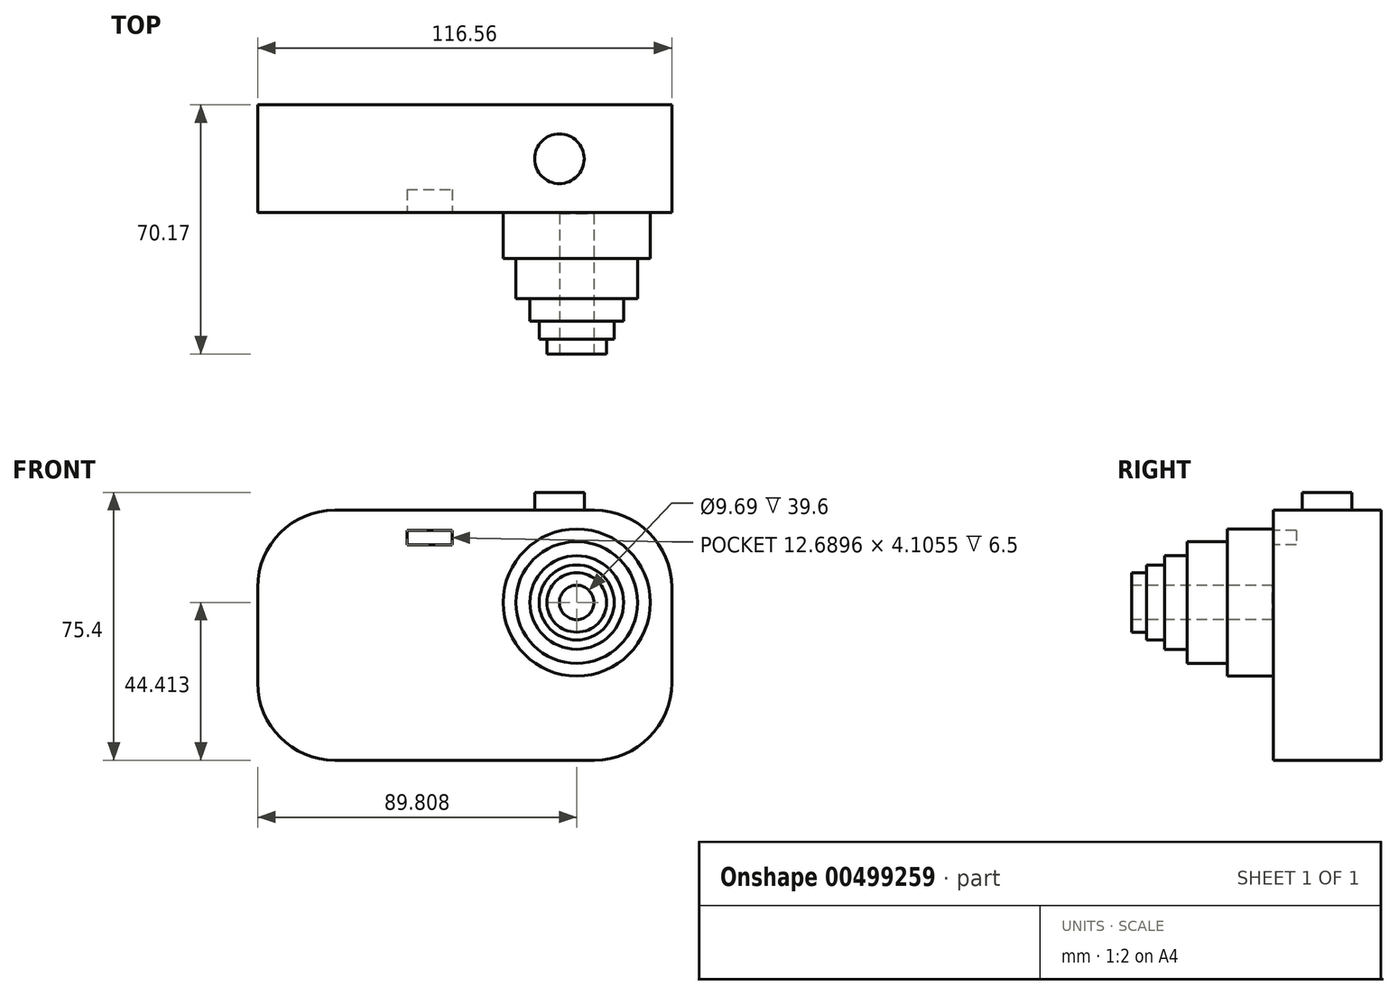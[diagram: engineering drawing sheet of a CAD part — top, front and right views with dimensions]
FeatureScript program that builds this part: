
annotation { "Feature Type Name" : "Feature", "Feature Type Description" : "" }
export const myFeature = defineFeature(function(context is Context, id is Id, definition is map)
    precondition{}
    {
        {
            var Q0;
            Q0=qCreatedBy(makeId("Top.planeOp"),FACE);
            var sketch = newSketch(context, id + "F0", { "sketchPlane" : qUnion([Q0])});
            skLineSegment(sketch, "E0.bottom", {"start": v(0, 0) * mm, "end": v(-116.56, 0) * mm});
            skLineSegment(sketch, "E0.top", {"start": v(0, 30.37) * mm, "end": v(-116.56, 30.37) * mm});
            skLineSegment(sketch, "E0.left", {"start": v(0, 0) * mm, "end": v(0, 30.37) * mm});
            skLineSegment(sketch, "E0.right", {"start": v(-116.56, 0) * mm, "end": v(-116.56, 30.37) * mm});
            skSolve(sketch);
        }
        {
            var Q0;
            Q0=makeQuery(id+"F0.imprint","IMPRINT",FACE,{"disambiguationData":[TD([[makeQuery(id+"F0.imprint","IMPRINT",EDGE,{"derivedFrom":sQuery(id+"F0.wireOp",EDGE,"E0.bottom")}),-1.0]])]});
            extrude(context, id + "F1", {"entities" : qUnion([Q0]), "depth" : 70.4 * mm});
        }
        {
            var Q0;
            Q0=makeQuery(id+"F1.opExtrude","CAP_EDGE",EDGE,{"disambiguationData":[OSD([sQuery(id+"F0.wireOp",EDGE,"E0.right")])],"isStart":false});
            var Q1;
            Q1=makeQuery(id+"F1.opExtrude","CAP_EDGE",EDGE,{"disambiguationData":[OSD([sQuery(id+"F0.wireOp",EDGE,"E0.left")])],"isStart":false});
            var Q2;
            Q2=makeQuery(id+"F1.opExtrude","CAP_EDGE",EDGE,{"disambiguationData":[OSD([sQuery(id+"F0.wireOp",EDGE,"E0.right")])],"isStart":true});
            var Q3;
            Q3=makeQuery(id+"F1.opExtrude","CAP_EDGE",EDGE,{"disambiguationData":[OSD([sQuery(id+"F0.wireOp",EDGE,"E0.left")])],"isStart":true});
            fillet(context, id + "F2", {"entities" : qUnion([Q0, Q1, Q2, Q3]), "radius" : 21.73 * mm, "tangentPropagation" : true, "allowEdgeOverflow" : false});
        }
        {
            var Q0;
            Q0=makeQuery(id+"F1.opExtrude","SWEPT_FACE",FACE,{"disambiguationData":[OSD([sQuery(id+"F0.wireOp",EDGE,"E0.bottom")])]});
            var sketch = newSketch(context, id + "F3", { "sketchPlane" : qUnion([Q0])});
            skCircle(sketch, "E1", {"center": v(-26.75, 44.41) * mm, "radius": 20.7 * mm});
            skSolve(sketch);
        }
        {
            var Q0;
            Q0=makeQuery(id+"F3.imprint","IMPRINT",FACE,{"disambiguationData":[TD([[makeQuery(id+"F3.imprint","IMPRINT",EDGE,{"derivedFrom":sQuery(id+"F3.wireOp",EDGE,"E1")}),1.0]])]});
            extrude(context, id + "F4", {"entities" : qUnion([Q0]), "operationType" : NewBodyOperationType.ADD, "depth" : 12.9 * mm});
        }
        {
            var Q0;
            Q0=makeQuery(id+"F4.opExtrude","CAP_FACE",FACE,{"disambiguationData":[OSD([sQuery(id+"F3.wireOp",EDGE,"E1")])],"isStart":false});
            var sketch = newSketch(context, id + "F5", { "sketchPlane" : qUnion([Q0])});
            skCircle(sketch, "E2", {"center": v(-26.75, 44.41) * mm, "radius": 17.15 * mm});
            skSolve(sketch);
        }
        {
            var Q0;
            Q0=makeQuery(id+"F5.imprint","IMPRINT",FACE,{"disambiguationData":[TD([[makeQuery(id+"F5.imprint","IMPRINT",EDGE,{"derivedFrom":sQuery(id+"F5.wireOp",EDGE,"E2")}),1.0]])]});
            extrude(context, id + "F6", {"entities" : qUnion([Q0]), "operationType" : NewBodyOperationType.ADD, "depth" : 11.3 * mm});
        }
        {
            var Q0;
            Q0=makeQuery(id+"F6.opExtrude","CAP_FACE",FACE,{"disambiguationData":[OSD([sQuery(id+"F5.wireOp",EDGE,"E2")])],"isStart":false});
            var sketch = newSketch(context, id + "F7", { "sketchPlane" : qUnion([Q0])});
            skCircle(sketch, "E3", {"center": v(-26.75, 44.41) * mm, "radius": 13.17 * mm});
            skSolve(sketch);
        }
        {
            var Q0;
            Q0=makeQuery(id+"F7.imprint","IMPRINT",FACE,{"disambiguationData":[TD([[makeQuery(id+"F7.imprint","IMPRINT",EDGE,{"derivedFrom":sQuery(id+"F7.wireOp",EDGE,"E3")}),1.0]])]});
            extrude(context, id + "F8", {"entities" : qUnion([Q0]), "operationType" : NewBodyOperationType.ADD, "depth" : 6.4 * mm});
        }
        {
            var Q0;
            Q0=makeQuery(id+"F8.opExtrude","CAP_FACE",FACE,{"disambiguationData":[OSD([sQuery(id+"F7.wireOp",EDGE,"E3")])],"isStart":false});
            var sketch = newSketch(context, id + "F9", { "sketchPlane" : qUnion([Q0])});
            skCircle(sketch, "E4", {"center": v(-26.75, 44.41) * mm, "radius": 10.56 * mm});
            skSolve(sketch);
        }
        {
            var Q0;
            Q0=makeQuery(id+"F9.imprint","IMPRINT",FACE,{"disambiguationData":[TD([[makeQuery(id+"F9.imprint","IMPRINT",EDGE,{"derivedFrom":sQuery(id+"F9.wireOp",EDGE,"E4")}),1.0]])]});
            extrude(context, id + "F10", {"entities" : qUnion([Q0]), "operationType" : NewBodyOperationType.ADD, "depth" : 5 * mm});
        }
        {
            var Q0;
            Q0=makeQuery(id+"F10.opExtrude","CAP_FACE",FACE,{"disambiguationData":[OSD([sQuery(id+"F9.wireOp",EDGE,"E4")])],"isStart":false});
            var sketch = newSketch(context, id + "F11", { "sketchPlane" : qUnion([Q0])});
            skCircle(sketch, "E5", {"center": v(-26.75, 44.41) * mm, "radius": 8.38 * mm});
            skSolve(sketch);
        }
        {
            var Q0;
            Q0=makeQuery(id+"F11.imprint","IMPRINT",FACE,{"disambiguationData":[TD([[makeQuery(id+"F11.imprint","IMPRINT",EDGE,{"derivedFrom":sQuery(id+"F11.wireOp",EDGE,"E5")}),1.0]])]});
            extrude(context, id + "F12", {"entities" : qUnion([Q0]), "operationType" : NewBodyOperationType.ADD, "depth" : 4.2 * mm});
        }
        {
            var Q0;
            Q0=makeQuery(id+"F1.opExtrude","SWEPT_FACE",FACE,{"disambiguationData":[OSD([sQuery(id+"F0.wireOp",EDGE,"E0.bottom")])]});
            var sketch = newSketch(context, id + "F13", { "sketchPlane" : qUnion([Q0])});
            skLineSegment(sketch, "E6.bottom", {"start": v(-59.49, 59.27) * mm, "end": v(-46.59, 59.27) * mm});
            skLineSegment(sketch, "E6.top", {"start": v(-59.49, 64.04) * mm, "end": v(-46.59, 64.04) * mm});
            skLineSegment(sketch, "E6.left", {"start": v(-59.49, 59.27) * mm, "end": v(-59.49, 64.04) * mm});
            skLineSegment(sketch, "E6.right", {"start": v(-46.59, 59.27) * mm, "end": v(-46.59, 64.04) * mm});
            skSolve(sketch);
        }
        {
            var Q0;
            Q0=makeQuery(id+"F13.imprint","IMPRINT",FACE,{"disambiguationData":[TD([[makeQuery(id+"F13.imprint","IMPRINT",EDGE,{"derivedFrom":sQuery(id+"F13.wireOp",EDGE,"E6.bottom")}),1.0]])]});
            extrude(context, id + "F14", {"entities" : qUnion([Q0]), "operationType" : NewBodyOperationType.ADD, "oppositeDirection" : true, "depth" : 6.7 * mm});
        }
        {
            var Q0;
            Q0=makeQuery(id+"F1.opExtrude","SWEPT_FACE",FACE,{"disambiguationData":[OSD([sQuery(id+"F0.wireOp",EDGE,"E0.bottom")])]});
            var sketch = newSketch(context, id + "F15", { "sketchPlane" : qUnion([Q0])});
            skLineSegment(sketch, "E7.bottom", {"start": v(-54.6, 62.77) * mm, "end": v(-68.2, 62.77) * mm});
            skLineSegment(sketch, "E7.top", {"start": v(-54.6, 58.14) * mm, "end": v(-68.2, 58.14) * mm});
            skLineSegment(sketch, "E7.left", {"start": v(-54.6, 62.77) * mm, "end": v(-54.6, 58.14) * mm});
            skLineSegment(sketch, "E7.right", {"start": v(-68.2, 62.77) * mm, "end": v(-68.2, 58.14) * mm});
            skSolve(sketch);
        }
        {
            var Q0;
            Q0=makeQuery(id+"F15.imprint","IMPRINT",FACE,{"disambiguationData":[TD([[makeQuery(id+"F15.imprint","IMPRINT",EDGE,{"derivedFrom":sQuery(id+"F15.wireOp",EDGE,"E7.bottom")}),1.0]])]});
            extrude(context, id + "F16", {"entities" : qUnion([Q0]), "operationType" : NewBodyOperationType.ADD, "oppositeDirection" : true, "depth" : 10 * mm});
        }
        {
            var Q0;
            Q0=makeQuery(id+"F1.opExtrude","SWEPT_FACE",FACE,{"disambiguationData":[OSD([sQuery(id+"F0.wireOp",EDGE,"E0.bottom")])]});
            var sketch = newSketch(context, id + "F17", { "sketchPlane" : qUnion([Q0])});
            skLineSegment(sketch, "E8.bottom", {"start": v(-74.52, 64.75) * mm, "end": v(-61.83, 64.75) * mm});
            skLineSegment(sketch, "E8.top", {"start": v(-74.52, 60.65) * mm, "end": v(-61.83, 60.65) * mm});
            skLineSegment(sketch, "E8.left", {"start": v(-74.52, 64.75) * mm, "end": v(-74.52, 60.65) * mm});
            skLineSegment(sketch, "E8.right", {"start": v(-61.83, 64.75) * mm, "end": v(-61.83, 60.65) * mm});
            skSolve(sketch);
        }
        {
            var Q0;
            Q0 = qSketchRegion(id + "F17", true);
            extrude(context, id + "F18", {"entities" : qUnion([Q0]), "operationType" : NewBodyOperationType.REMOVE, "oppositeDirection" : true, "depth" : 6.5 * mm});
        }
        {
            var Q0;
            Q0=makeQuery(id+"F1.opExtrude","CAP_FACE",FACE,{"disambiguationData":[OSD([sQuery(id+"F0.wireOp",EDGE,"E0.bottom"),sQuery(id+"F0.wireOp",EDGE,"E0.top"),sQuery(id+"F0.wireOp",EDGE,"E0.left"),sQuery(id+"F0.wireOp",EDGE,"E0.right")])],"isStart":false});
            var sketch = newSketch(context, id + "F19", { "sketchPlane" : qUnion([Q0])});
            skCircle(sketch, "E9", {"center": v(-31.62, 15.18) * mm, "radius": 6.98 * mm});
            skSolve(sketch);
        }
        {
            var Q0;
            Q0=makeQuery(id+"F19.imprint","IMPRINT",FACE,{"disambiguationData":[TD([[makeQuery(id+"F19.imprint","IMPRINT",EDGE,{"derivedFrom":sQuery(id+"F19.wireOp",EDGE,"E9")}),1.0]])]});
            extrude(context, id + "F20", {"entities" : qUnion([Q0]), "operationType" : NewBodyOperationType.ADD, "depth" : 5 * mm});
        }
        {
            var Q0;
            Q0=makeQuery(id+"F12.opExtrude","CAP_FACE",FACE,{"disambiguationData":[OSD([sQuery(id+"F11.wireOp",EDGE,"E5")])],"isStart":false});
            var sketch = newSketch(context, id + "F21", { "sketchPlane" : qUnion([Q0])});
            skCircle(sketch, "E10", {"center": v(-26.75, 44.41) * mm, "radius": 4.85 * mm});
            skSolve(sketch);
        }
        {
            var Q0;
            Q0=makeQuery(id+"F21.imprint","IMPRINT",FACE,{"disambiguationData":[TD([[makeQuery(id+"F21.imprint","IMPRINT",EDGE,{"derivedFrom":sQuery(id+"F21.wireOp",EDGE,"E10")}),1.0]])]});
            extrude(context, id + "F22", {"entities" : qUnion([Q0]), "operationType" : NewBodyOperationType.REMOVE, "oppositeDirection" : true, "depth" : 39.6 * mm});
        }
    });
